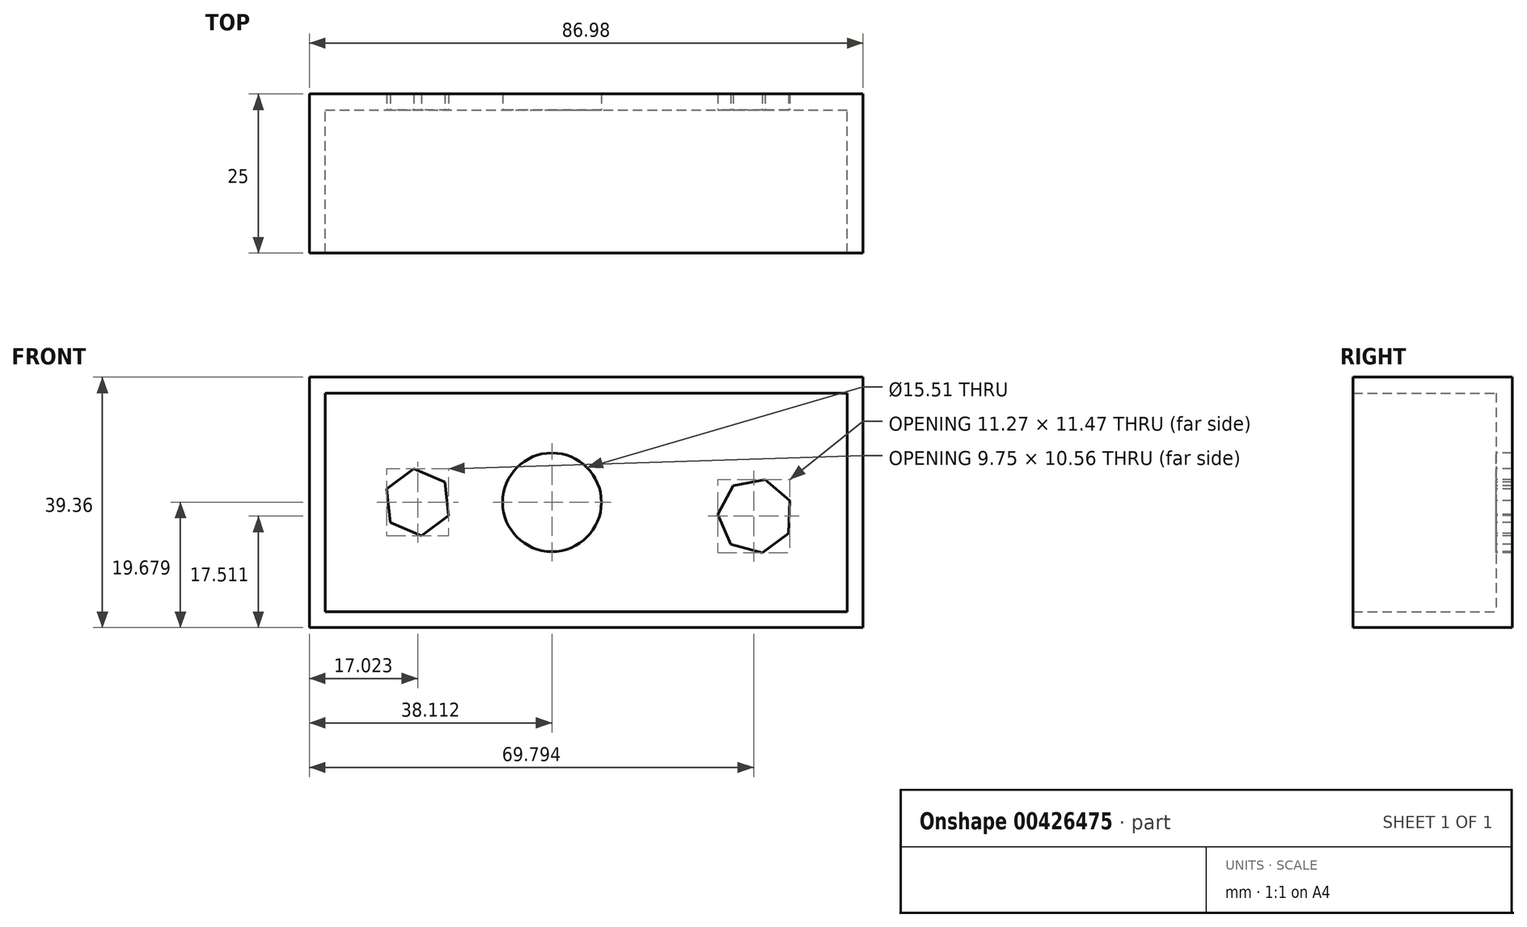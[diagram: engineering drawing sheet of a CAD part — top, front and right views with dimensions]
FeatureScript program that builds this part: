
annotation { "Feature Type Name" : "Feature", "Feature Type Description" : "" }
export const myFeature = defineFeature(function(context is Context, id is Id, definition is map)
    precondition{}
    {
        {
            var Q0;
            Q0=qCreatedBy(makeId("Front.planeOp"),FACE);
            var sketch = newSketch(context, id + "F0", { "sketchPlane" : qUnion([Q0])});
            skLineSegment(sketch, "E0.bottom", {"start": v(-136.64, 18.98) * mm, "end": v(-49.66, 18.98) * mm});
            skLineSegment(sketch, "E0.top", {"start": v(-136.64, -20.38) * mm, "end": v(-49.66, -20.38) * mm});
            skLineSegment(sketch, "E0.left", {"start": v(-136.64, 18.98) * mm, "end": v(-136.64, -20.38) * mm});
            skLineSegment(sketch, "E0.right", {"start": v(-49.66, 18.98) * mm, "end": v(-49.66, -20.38) * mm});
            skSolve(sketch);
        }
        {
            var Q0;
            Q0=makeQuery(id+"F0.imprint","IMPRINT",FACE,{"disambiguationData":[TD([[makeQuery(id+"F0.imprint","IMPRINT",EDGE,{"derivedFrom":sQuery(id+"F0.wireOp",EDGE,"E0.bottom")}),-1.0]])]});
            extrude(context, id + "F1", {"entities" : qUnion([Q0]), "depth" : 25 * mm});
        }
        {
            var Q0;
            Q0=makeQuery(id+"F1.opExtrude","CAP_FACE",FACE,{"disambiguationData":[OSD([sQuery(id+"F0.wireOp",EDGE,"E0.bottom"),sQuery(id+"F0.wireOp",EDGE,"E0.top"),sQuery(id+"F0.wireOp",EDGE,"E0.left"),sQuery(id+"F0.wireOp",EDGE,"E0.right")])],"isStart":false});
            shell(context, id + "F2", {"entities" : qUnion([Q0]), "thickness" : 2.5 * mm});
        }
        {
            var Q0;
            Q0=makeQuery(id+"F2.opShell","OFFSET_FACE",FACE,{"disambiguationData":[OSD([sQuery(id+"F0.wireOp",EDGE,"E0.bottom"),sQuery(id+"F0.wireOp",EDGE,"E0.top"),sQuery(id+"F0.wireOp",EDGE,"E0.left"),sQuery(id+"F0.wireOp",EDGE,"E0.right")])]});
            var sketch = newSketch(context, id + "F3", { "sketchPlane" : qUnion([Q0])});
            skCircle(sketch, "E1", {"center": v(-98.53, -0.7) * mm, "radius": 7.76 * mm});
            skPoint(sketch, "E1.centerSnap0", {"position": v(-134.14, -0.7) * mm});
            skSolve(sketch);
        }
        {
            var Q0;
            Q0 = qSketchRegion(id + "F3", true);
            extrude(context, id + "F4", {"entities" : qUnion([Q0]), "operationType" : NewBodyOperationType.REMOVE, "oppositeDirection" : true, "depth" : 25 * mm});
        }
        {
            var Q0;
            Q0=makeQuery(id+"F2.opShell","OFFSET_FACE",FACE,{"disambiguationData":[OSD([sQuery(id+"F0.wireOp",EDGE,"E0.bottom"),sQuery(id+"F0.wireOp",EDGE,"E0.top"),sQuery(id+"F0.wireOp",EDGE,"E0.left"),sQuery(id+"F0.wireOp",EDGE,"E0.right")])]});
            var sketch = newSketch(context, id + "F5", { "sketchPlane" : qUnion([Q0])});
            skCircle(sketch, "E2.cCircle", {"center": v(-119.62, -0.7) * mm, "radius": 4.6 * mm, "construction": true});
            skPoint(sketch, "E2.cCircle.centerSnap0", {"position": v(-134.14, -0.7) * mm});
            skLineSegment(sketch, "E2.0", {"start": v(-114.74, -2.82) * mm, "end": v(-119.02, -5.98) * mm});
            skLineSegment(sketch, "E2.1", {"start": v(-119.02, -5.98) * mm, "end": v(-123.89, -3.86) * mm});
            skLineSegment(sketch, "E2.2", {"start": v(-123.89, -3.86) * mm, "end": v(-124.49, 1.42) * mm});
            skLineSegment(sketch, "E2.3", {"start": v(-124.49, 1.42) * mm, "end": v(-120.22, 4.58) * mm});
            skLineSegment(sketch, "E2.4", {"start": v(-120.22, 4.58) * mm, "end": v(-115.34, 2.46) * mm});
            skLineSegment(sketch, "E2.5", {"start": v(-115.34, 2.46) * mm, "end": v(-114.74, -2.82) * mm});
            skPoint(sketch, "E2.0.midPoint", {"position": v(-116.88, -4.4) * mm});
            skCircle(sketch, "E3.cCircle", {"center": v(-66.6, -2.82) * mm, "radius": 5.3 * mm, "construction": true});
            skLineSegment(sketch, "E3.0", {"start": v(-61.4, -5.57) * mm, "end": v(-65.5, -8.6) * mm});
            skLineSegment(sketch, "E3.1", {"start": v(-65.5, -8.6) * mm, "end": v(-70.44, -7.29) * mm});
            skLineSegment(sketch, "E3.2", {"start": v(-70.44, -7.29) * mm, "end": v(-72.48, -2.6) * mm});
            skLineSegment(sketch, "E3.3", {"start": v(-72.48, -2.6) * mm, "end": v(-70.1, 1.91) * mm});
            skLineSegment(sketch, "E3.4", {"start": v(-70.1, 1.91) * mm, "end": v(-65.08, 2.87) * mm});
            skLineSegment(sketch, "E3.5", {"start": v(-65.08, 2.87) * mm, "end": v(-61.2, -0.46) * mm});
            skLineSegment(sketch, "E3.6", {"start": v(-61.2, -0.46) * mm, "end": v(-61.4, -5.57) * mm});
            skPoint(sketch, "E3.0.midPoint", {"position": v(-63.45, -7.09) * mm});
            skSolve(sketch);
        }
        {
            var Q0;
            Q0 = qSketchRegion(id + "F5", true);
            extrude(context, id + "F6", {"entities" : qUnion([Q0]), "operationType" : NewBodyOperationType.REMOVE, "oppositeDirection" : true, "depth" : 25 * mm});
        }
    });
